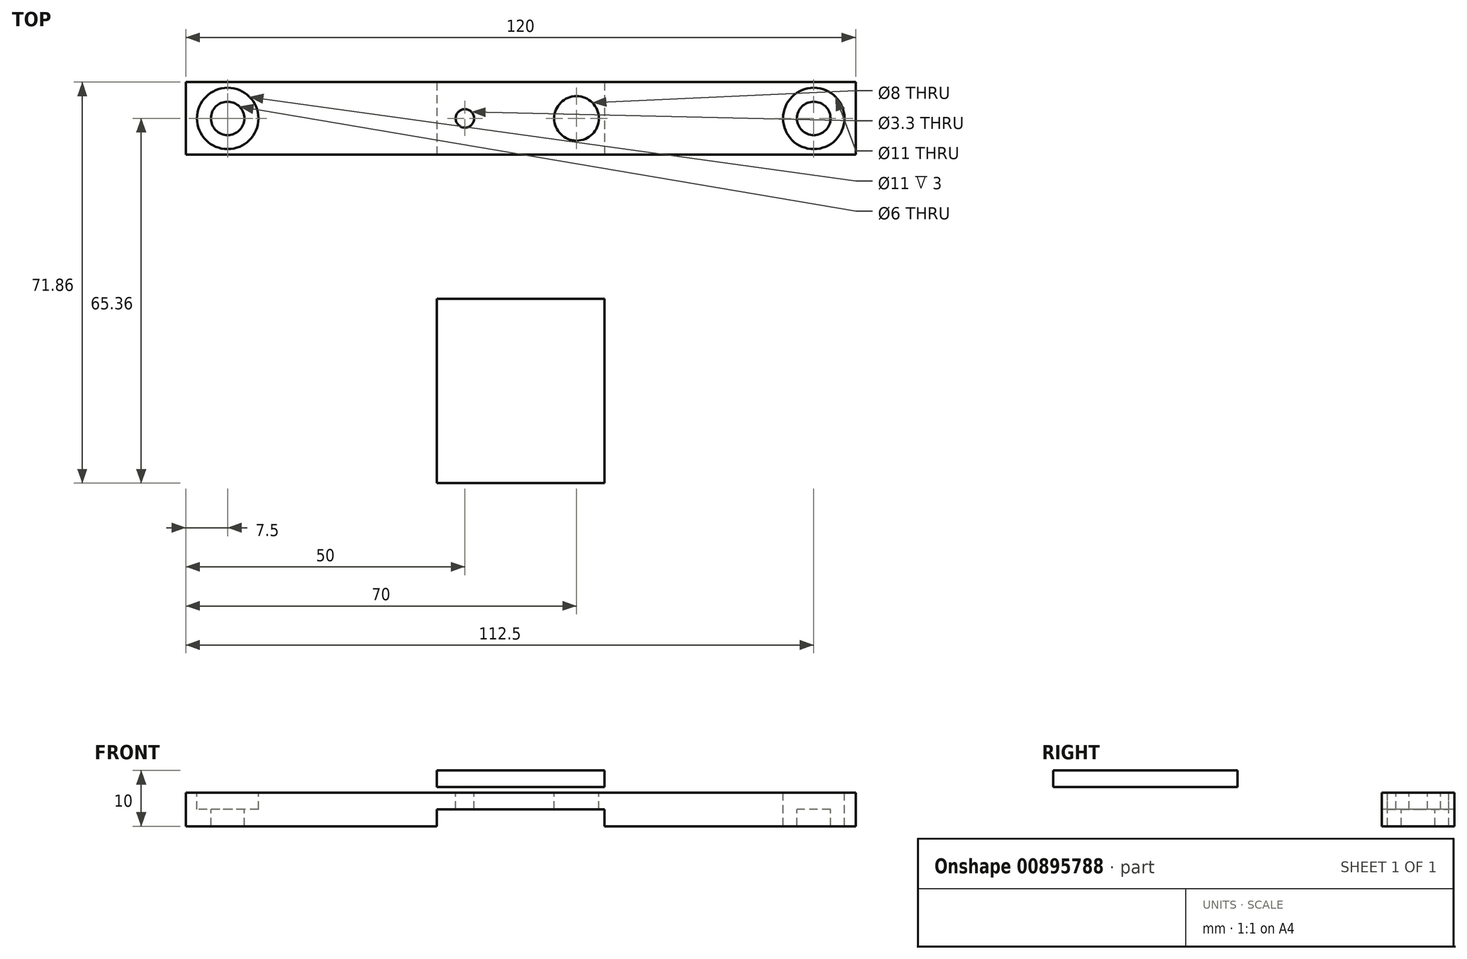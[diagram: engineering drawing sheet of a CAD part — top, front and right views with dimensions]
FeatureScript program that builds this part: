
annotation { "Feature Type Name" : "Feature", "Feature Type Description" : "" }
export const myFeature = defineFeature(function(context is Context, id is Id, definition is map)
    precondition{}
    {
        {
            var Q0;
            Q0=qCreatedBy(makeId("Top.planeOp"),FACE);
            var sketch = newSketch(context, id + "F0", { "sketchPlane" : qUnion([Q0])});
            skLineSegment(sketch, "E0.bottom", {"start": v(-60, 6.5) * mm, "end": v(60, 6.5) * mm});
            skLineSegment(sketch, "E0.top", {"start": v(-60, -6.5) * mm, "end": v(60, -6.5) * mm});
            skLineSegment(sketch, "E0.left", {"start": v(-60, 6.5) * mm, "end": v(-60, -6.5) * mm});
            skLineSegment(sketch, "E0.right", {"start": v(60, 6.5) * mm, "end": v(60, -6.5) * mm});
            skPoint(sketch, "E0.middle", {"position": v(0, 0) * mm});
            skLineSegment(sketch, "E1.bottom", {"start": v(-52.5, 3) * mm, "end": v(-52.5, 3) * mm});
            skLineSegment(sketch, "E1.top", {"start": v(-52.5, -3) * mm, "end": v(-52.5, -3) * mm});
            skLineSegment(sketch, "E1.left", {"start": v(-49.5, 0) * mm, "end": v(-49.5, 0) * mm});
            skLineSegment(sketch, "E1.right", {"start": v(-55.5, 0) * mm, "end": v(-55.5, 0) * mm});
            skPoint(sketch, "E1.middle", {"position": v(-52.5, 0) * mm});
            skPoint(sketch, "E2.visualSharp", {"position": v(-55.5, 3) * mm});
            skArc(sketch, "E2.filletArc", {"start": v(-52.5, 3) * mm, "mid": v(-54.62, 2.12) * mm, "end": v(-55.5, 0) * mm});
            skPoint(sketch, "E3.visualSharp", {"position": v(-49.5, 3) * mm});
            skArc(sketch, "E3.filletArc", {"start": v(-49.5, 0) * mm, "mid": v(-50.38, 2.12) * mm, "end": v(-52.5, 3) * mm});
            skPoint(sketch, "E4.visualSharp", {"position": v(-49.5, -3) * mm});
            skArc(sketch, "E4.filletArc", {"start": v(-52.5, -3) * mm, "mid": v(-50.38, -2.12) * mm, "end": v(-49.5, 0) * mm});
            skPoint(sketch, "E5.visualSharp", {"position": v(-55.5, -3) * mm});
            skArc(sketch, "E5.filletArc", {"start": v(-55.5, 0) * mm, "mid": v(-54.62, -2.12) * mm, "end": v(-52.5, -3) * mm});
            skPoint(sketch, "E6.right.end.orphan", {"position": v(0, -6.5) * mm});
            skCircle(sketch, "E7", {"center": v(-52.5, 0) * mm, "radius": 5.5 * mm});
            skArc(sketch, "E8.MirrorCS", {"start": v(55.5, 0) * mm, "mid": v(54.62, -2.12) * mm, "end": v(52.5, -3) * mm});
            skArc(sketch, "E9.MirrorCS", {"start": v(52.5, 3) * mm, "mid": v(54.62, 2.12) * mm, "end": v(55.5, 0) * mm});
            skArc(sketch, "E10.MirrorCS", {"start": v(52.5, -3) * mm, "mid": v(50.38, -2.12) * mm, "end": v(49.5, 0) * mm});
            skArc(sketch, "E11.MirrorCS", {"start": v(49.5, 0) * mm, "mid": v(50.38, 2.12) * mm, "end": v(52.5, 3) * mm});
            skLineSegment(sketch, "E12.MirrorCS", {"start": v(55.5, 0) * mm, "end": v(55.5, 0) * mm});
            skLineSegment(sketch, "E13.MirrorCS", {"start": v(52.5, 3) * mm, "end": v(52.5, 3) * mm});
            skPoint(sketch, "E14.MirrorP", {"position": v(49.5, -3) * mm});
            skPoint(sketch, "E15.MirrorP", {"position": v(49.5, 3) * mm});
            skLineSegment(sketch, "E16.MirrorCS", {"start": v(52.5, -3) * mm, "end": v(52.5, -3) * mm});
            skPoint(sketch, "E17.MirrorP", {"position": v(55.5, 3) * mm});
            skPoint(sketch, "E18.MirrorP", {"position": v(55.5, -3) * mm});
            skCircle(sketch, "E19.MirrorC", {"center": v(52.5, 0) * mm, "radius": 5.5 * mm});
            skLineSegment(sketch, "E20.MirrorCS", {"start": v(49.5, 0) * mm, "end": v(49.5, 0) * mm});
            skCircle(sketch, "E21", {"center": v(-10, 0) * mm, "radius": 1.65 * mm});
            skCircle(sketch, "E22", {"center": v(-10, 0) * mm, "radius": 4 * mm});
            skCircle(sketch, "E23.MirrorC", {"center": v(10, 0) * mm, "radius": 4 * mm});
            skCircle(sketch, "E24.MirrorC", {"center": v(10, 0) * mm, "radius": 1.65 * mm});
            skLineSegment(sketch, "E25.bottom", {"start": v(-15, -32.36) * mm, "end": v(15, -32.36) * mm});
            skLineSegment(sketch, "E25.top", {"start": v(-15, -65.36) * mm, "end": v(15, -65.36) * mm});
            skLineSegment(sketch, "E25.left", {"start": v(-15, -32.36) * mm, "end": v(-15, -65.36) * mm});
            skLineSegment(sketch, "E25.right", {"start": v(15, -32.36) * mm, "end": v(15, -65.36) * mm});
            skPoint(sketch, "E25.middle", {"position": v(0, -48.86) * mm});
            skSolve(sketch);
        }
        {
            var Q0;
            Q0=makeQuery(id+"F0.imprint","IMPRINT",FACE,{"disambiguationData":[TD([[makeQuery(id+"F0.imprint","IMPRINT",EDGE,{"derivedFrom":sQuery(id+"F0.wireOp",EDGE,"E0.bottom")}),-1.0]])]});
            var Q1;
            Q1=makeQuery(id+"F0.imprint","IMPRINT",FACE,{"disambiguationData":[TD([[makeQuery(id+"F0.imprint","IMPRINT",EDGE,{"derivedFrom":sQuery(id+"F0.wireOp",EDGE,"E1.left")}),1.0]])]});
            var Q2;
            Q2=makeQuery(id+"F0.imprint","IMPRINT",FACE,{"disambiguationData":[TD([[makeQuery(id+"F0.imprint","IMPRINT",EDGE,{"derivedFrom":sQuery(id+"F0.wireOp",EDGE,"66f1095f-65f3-4b51-a908-25b2928926180.MirrorCS")}),1.0]])]});
            var Q3;
            Q3=makeQuery(id+"F0.imprint","IMPRINT",FACE,{"disambiguationData":[TD([[makeQuery(id+"F0.imprint","IMPRINT",EDGE,{"derivedFrom":sQuery(id+"F0.wireOp",EDGE,"E2.filletArc")}),-1.0]])]});
            var Q4;
            Q4=makeQuery(id+"F0.imprint","IMPRINT",FACE,{"disambiguationData":[TD([[makeQuery(id+"F0.imprint","IMPRINT",EDGE,{"derivedFrom":sQuery(id+"F0.wireOp",EDGE,"E8.MirrorCS")}),1.0]])]});
            var Q5;
            Q5=makeQuery(id+"F0.imprint","IMPRINT",FACE,{"disambiguationData":[TD([[makeQuery(id+"F0.imprint","IMPRINT",EDGE,{"derivedFrom":sQuery(id+"F0.wireOp",EDGE,"E21")}),-1.0]])]});
            var Q6;
            Q6=makeQuery(id+"F0.imprint","IMPRINT",FACE,{"disambiguationData":[TD([[makeQuery(id+"F0.imprint","IMPRINT",EDGE,{"derivedFrom":sQuery(id+"F0.wireOp",EDGE,"E23.MirrorC")}),-1.0]])]});
            extrude(context, id + "F1", {"entities" : qUnion([Q0, Q1, Q2, Q3, Q4, Q5, Q6]), "oppositeDirection" : true, "depth" : 10 * mm, "offsetDistance" : 25 * mm});
        }
        {
            var Q0;
            Q0=makeQuery(id+"F0.imprint","IMPRINT",FACE,{"disambiguationData":[TD([[makeQuery(id+"F0.imprint","IMPRINT",EDGE,{"derivedFrom":sQuery(id+"F0.wireOp",EDGE,"E1.left")}),-1.0]])]});
            var Q1;
            Q1=makeQuery(id+"F0.imprint","IMPRINT",FACE,{"disambiguationData":[TD([[makeQuery(id+"F0.imprint","IMPRINT",EDGE,{"derivedFrom":sQuery(id+"F0.wireOp",EDGE,"66f1095f-65f3-4b51-a908-25b2928926180.MirrorCS")}),-1.0]])]});
            var Q2;
            Q2=makeQuery(id+"F0.imprint","IMPRINT",FACE,{"disambiguationData":[TD([[makeQuery(id+"F0.imprint","IMPRINT",EDGE,{"derivedFrom":sQuery(id+"F0.wireOp",EDGE,"66f1095f-65f3-4b51-a908-25b2928926180.MirrorCS")}),1.0]])]});
            var Q3;
            Q3=makeQuery(id+"F0.imprint","IMPRINT",FACE,{"disambiguationData":[TD([[makeQuery(id+"F0.imprint","IMPRINT",EDGE,{"derivedFrom":sQuery(id+"F0.wireOp",EDGE,"E1.left")}),1.0]])]});
            var Q4;
            Q4=makeQuery(id+"F0.imprint","IMPRINT",FACE,{"disambiguationData":[TD([[makeQuery(id+"F0.imprint","IMPRINT",EDGE,{"derivedFrom":sQuery(id+"F0.wireOp",EDGE,"E2.filletArc")}),-1.0]])]});
            var Q5;
            Q5=makeQuery(id+"F0.imprint","IMPRINT",FACE,{"disambiguationData":[TD([[makeQuery(id+"F0.imprint","IMPRINT",EDGE,{"derivedFrom":sQuery(id+"F0.wireOp",EDGE,"E8.MirrorCS")}),1.0]])]});
            extrude(context, id + "F2", {"entities" : qUnion([Q0, Q1, Q2, Q3, Q4, Q5]), "operationType" : NewBodyOperationType.REMOVE, "oppositeDirection" : true, "depth" : 7 * mm, "offsetDistance" : 25 * mm});
        }
        {
            var Q0;
            Q0=makeQuery(id+"F1.opExtrude","SWEPT_FACE",FACE,{"disambiguationData":[OSD([sQuery(id+"F0.wireOp",EDGE,"E0.top")])]});
            var sketch = newSketch(context, id + "F3", { "sketchPlane" : qUnion([Q0])});
            skLineSegment(sketch, "E26.bottom", {"start": v(0, -10) * mm, "end": v(-15, -10) * mm});
            skLineSegment(sketch, "E26.top", {"start": v(0, -7) * mm, "end": v(-15, -7) * mm});
            skLineSegment(sketch, "E26.right", {"start": v(-15, -10) * mm, "end": v(-15, -7) * mm});
            skLineSegment(sketch, "E27.MirrorCS", {"start": v(15, -10) * mm, "end": v(15, -7) * mm});
            skLineSegment(sketch, "E28.MirrorCS", {"start": v(0, -7) * mm, "end": v(15, -7) * mm});
            skLineSegment(sketch, "E29.MirrorCS", {"start": v(0, -10) * mm, "end": v(15, -10) * mm});
            skSolve(sketch);
        }
        {
            var Q0;
            Q0 = qSketchRegion(id + "F3", true);
            extrude(context, id + "F4", {"entities" : qUnion([Q0]), "operationType" : NewBodyOperationType.REMOVE, "oppositeDirection" : true, "depth" : 25 * mm, "offsetDistance" : 25 * mm});
        }
        {
            var Q0;
            Q0=makeQuery(id+"F0.imprint","IMPRINT",FACE,{"disambiguationData":[TD([[makeQuery(id+"F0.imprint","IMPRINT",EDGE,{"derivedFrom":sQuery(id+"F0.wireOp",EDGE,"E21")}),-1.0]])]});
            var Q1;
            Q1=makeQuery(id+"F0.imprint","IMPRINT",FACE,{"disambiguationData":[TD([[makeQuery(id+"F0.imprint","IMPRINT",EDGE,{"derivedFrom":sQuery(id+"F0.wireOp",EDGE,"E23.MirrorC")}),-1.0]])]});
            extrude(context, id + "F5", {"entities" : qUnion([Q0, Q1]), "operationType" : NewBodyOperationType.REMOVE, "oppositeDirection" : true, "depth" : 4 * mm, "offsetDistance" : 25 * mm});
        }
        {
            var Q0;
            Q0=makeQuery(id+"F0.imprint","IMPRINT",FACE,{"disambiguationData":[TD([[makeQuery(id+"F0.imprint","IMPRINT",EDGE,{"derivedFrom":sQuery(id+"F0.wireOp",EDGE,"E25.bottom")}),-1.0]])]});
            extrude(context, id + "F6", {"entities" : qUnion([Q0]), "oppositeDirection" : true, "depth" : 3 * mm, "offsetDistance" : 25 * mm});
        }
    });
